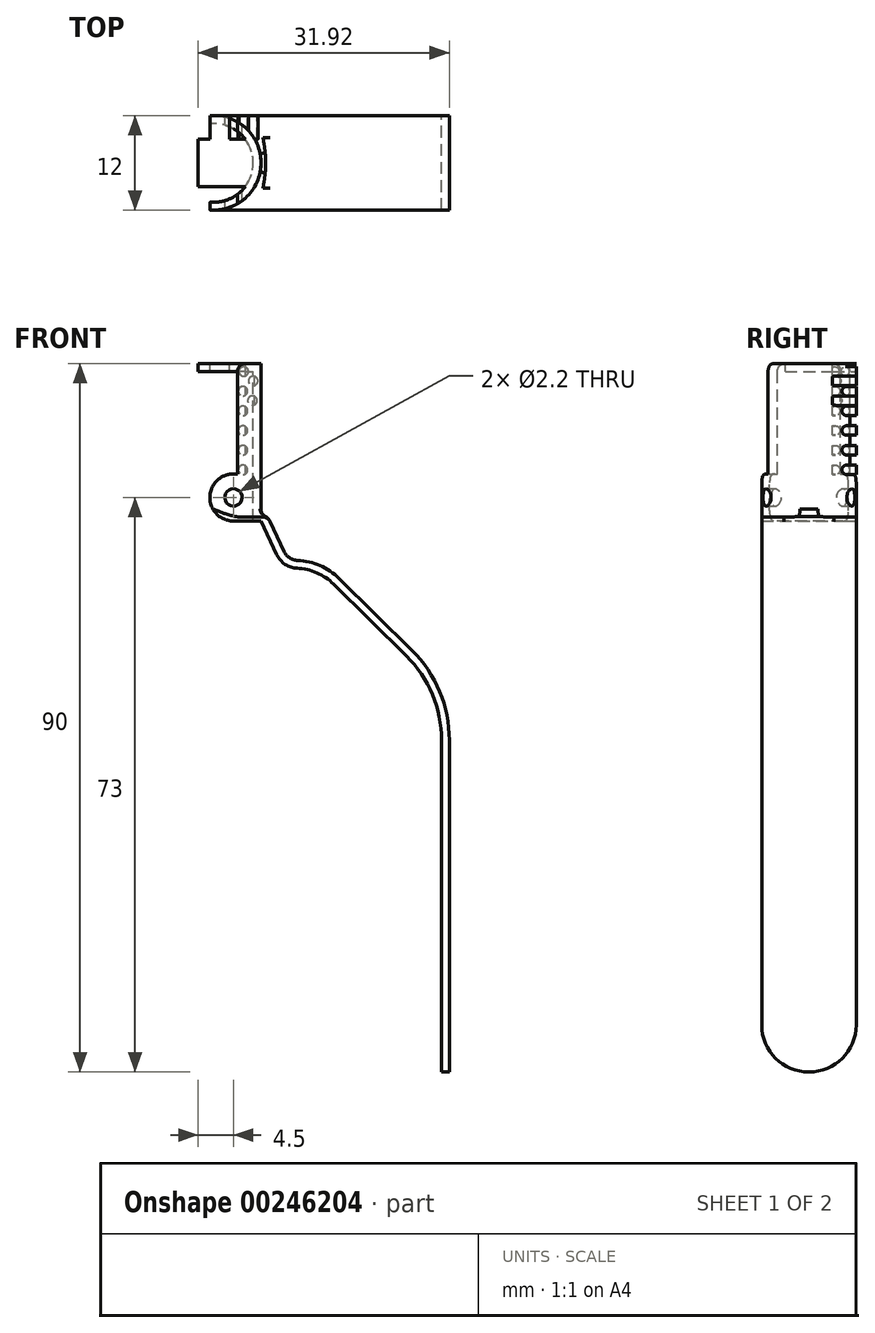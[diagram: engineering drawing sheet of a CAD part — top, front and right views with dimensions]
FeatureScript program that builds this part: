
annotation { "Feature Type Name" : "Feature", "Feature Type Description" : "" }
export const myFeature = defineFeature(function(context is Context, id is Id, definition is map)
    precondition{}
    {
        {
            var Q0;
            Q0=qCreatedBy(makeId("Front.planeOp"),FACE);
            var sketch = newSketch(context, id + "F0", { "sketchPlane" : qUnion([Q0])});
            skLineSegment(sketch, "E0", {"start": v(-3, 6) * mm, "end": v(-3, 20) * mm});
            skLineSegment(sketch, "E1", {"start": v(-3, 20) * mm, "end": v(0, 20) * mm});
            skLineSegment(sketch, "E2", {"start": v(0, 20) * mm, "end": v(0, 2.36) * mm});
            skLineSegment(sketch, "E3", {"start": v(0, 0) * mm, "end": v(-3.5, 0) * mm});
            skArc(sketch, "E4", {"start": v(-3.5, 0) * mm, "mid": v(-6.5, 3) * mm, "end": v(-3.5, 6) * mm});
            skLineSegment(sketch, "E5", {"start": v(-3.5, 6) * mm, "end": v(-3, 6) * mm});
            skLineSegment(sketch, "E6", {"start": v(0, 0) * mm, "end": v(2, -4.27) * mm});
            skArc(sketch, "E7", {"start": v(2, -4.27) * mm, "mid": v(3.05, -5.5) * mm, "end": v(4.6, -6) * mm});
            skArc(sketch, "E8", {"start": v(4.6, -6) * mm, "mid": v(7.1, -6.57) * mm, "end": v(9.22, -8.01) * mm});
            skLineSegment(sketch, "E9", {"start": v(9.22, -8.01) * mm, "end": v(18.47, -17.15) * mm});
            skArc(sketch, "E10", {"start": v(18.47, -17.15) * mm, "mid": v(21.76, -22.04) * mm, "end": v(22.92, -27.82) * mm});
            skLineSegment(sketch, "E11", {"start": v(22.92, -27.82) * mm, "end": v(22.92, -70) * mm});
            skLineSegment(sketch, "E12", {"start": v(0, 2.36) * mm, "end": v(2.62, -3.24) * mm});
            skLineSegment(sketch, "E13", {"start": v(9.92, -7.3) * mm, "end": v(19.17, -16.44) * mm});
            skArc(sketch, "E14", {"start": v(19.17, -16.44) * mm, "mid": v(22.68, -21.66) * mm, "end": v(23.92, -27.82) * mm});
            skLineSegment(sketch, "E15", {"start": v(23.92, -27.82) * mm, "end": v(23.92, -58.92) * mm});
            skArc(sketch, "E16", {"start": v(9.92, -7.3) * mm, "mid": v(7.5, -5.66) * mm, "end": v(4.63, -5) * mm});
            skArc(sketch, "E17", {"start": v(4.63, -5) * mm, "mid": v(3.6, -4.66) * mm, "end": v(2.9, -3.85) * mm});
            skLineSegment(sketch, "E18", {"start": v(2.9, -3.85) * mm, "end": v(2.62, -3.24) * mm});
            skLineSegment(sketch, "E19", {"start": v(23.92, -58.92) * mm, "end": v(23.92, -70) * mm});
            skLineSegment(sketch, "E20", {"start": v(22.92, -70) * mm, "end": v(23.92, -70) * mm});
            skCircle(sketch, "E21", {"center": v(-3.5, 3) * mm, "radius": 1.1 * mm});
            skSolve(sketch);
        }
        {
            var Q0;
            Q0=makeQuery(id+"F0.imprint","IMPRINT",FACE,{"disambiguationData":[TD([[makeQuery(id+"F0.imprint","IMPRINT",EDGE,{"derivedFrom":sQuery(id+"F0.wireOp",EDGE,"E0")}),-1.0]])]});
            extrude(context, id + "F1", {"entities" : qUnion([Q0]), "endBound" : BoundingType.SYMMETRIC, "depth" : 12 * mm});
        }
        {
            var Q0;
            Q0=makeQuery(id+"F1.opExtrude","CAP_EDGE",EDGE,{"disambiguationData":[OSD([sQuery(id+"F0.wireOp",EDGE,"E20")])],"isStart":false});
            var Q1;
            Q1=makeQuery(id+"F1.opExtrude","CAP_EDGE",EDGE,{"disambiguationData":[OSD([sQuery(id+"F0.wireOp",EDGE,"E20")])],"isStart":true});
            fillet(context, id + "F2", {"entities" : qUnion([Q0, Q1]), "radius" : 6 * mm, "tangentPropagation" : true, "allowEdgeOverflow" : false});
        }
        {
            var Q0;
            Q0=makeQuery(id+"F1.opExtrude","SWEPT_FACE",FACE,{"disambiguationData":[OSD([sQuery(id+"F0.wireOp",EDGE,"E1")])]});
            var sketch = newSketch(context, id + "F3", { "sketchPlane" : qUnion([Q0])});
            skArc(sketch, "E22", {"start": v(-6, -6) * mm, "mid": v(0, 0) * mm, "end": v(-6, 6) * mm});
            skLineSegment(sketch, "E23", {"start": v(1, -6) * mm, "end": v(-7.5, -6) * mm});
            skPoint(sketch, "E23.endSnap0", {"position": v(-1.5, -6) * mm});
            skLineSegment(sketch, "E24", {"start": v(1, 6) * mm, "end": v(-7.5, 6) * mm});
            skLineSegment(sketch, "E25", {"start": v(1, 6) * mm, "end": v(1, -6) * mm});
            skArc(sketch, "E26", {"start": v(-6, 5) * mm, "mid": v(-1, 0) * mm, "end": v(-6, -5) * mm});
            skLineSegment(sketch, "E27", {"start": v(-6, 5) * mm, "end": v(-7.5, 5) * mm});
            skLineSegment(sketch, "E28", {"start": v(-6, -5) * mm, "end": v(-7.5, -5) * mm});
            skLineSegment(sketch, "E29", {"start": v(-7.5, 5) * mm, "end": v(-7.5, -5) * mm});
            skSolve(sketch);
        }
        {
            var Q0;
            Q0 = qSketchRegion(id + "F3", true);
            extrude(context, id + "F4", {"entities" : qUnion([Q0]), "operationType" : NewBodyOperationType.REMOVE, "oppositeDirection" : true, "depth" : 19.5 * mm});
        }
        {
            var Q0;
            Q0=makeQuery(id+"F4.boolean.opBoolean","COPY",FACE,{"derivedFrom":makeQuery(id+"F4.opExtrude","CAP_FACE",FACE,{"disambiguationData":[OSD([sQuery(id+"F3.wireOp",EDGE,"E26"),sQuery(id+"F3.wireOp",EDGE,"E27"),sQuery(id+"F3.wireOp",EDGE,"E28"),sQuery(id+"F3.wireOp",EDGE,"E29")])],"isStart":false})});
            var sketch = newSketch(context, id + "F5", { "sketchPlane" : qUnion([Q0])});
            skArc(sketch, "E30", {"start": v(-5.16, -4.93) * mm, "mid": v(-1, 0) * mm, "end": v(-5.16, 4.93) * mm});
            skLineSegment(sketch, "E31", {"start": v(-5.16, 4.93) * mm, "end": v(-5.16, -4.93) * mm});
            skSolve(sketch);
        }
        {
            var Q0;
            Q0 = qSketchRegion(id + "F5", true);
            extrude(context, id + "F6", {"entities" : qUnion([Q0]), "operationType" : NewBodyOperationType.REMOVE, "oppositeDirection" : true, "depth" : 2 * mm});
        }
        {
            var Q0;
            Q0=makeQuery(id+"F1.opExtrude","SWEPT_FACE",FACE,{"disambiguationData":[OSD([sQuery(id+"F0.wireOp",EDGE,"E1")])]});
            var sketch = newSketch(context, id + "F7", { "sketchPlane" : qUnion([Q0])});
            skArc(sketch, "E32", {"start": v(-2, -3) * mm, "mid": v(-1, 0) * mm, "end": v(-2, 3) * mm});
            skLineSegment(sketch, "E33", {"start": v(-2, 3) * mm, "end": v(-8, 3) * mm});
            skLineSegment(sketch, "E34", {"start": v(-2, -3) * mm, "end": v(-8, -3) * mm});
            skLineSegment(sketch, "E35", {"start": v(-8, -3) * mm, "end": v(-8, 3) * mm});
            skSolve(sketch);
        }
        {
            var Q0;
            Q0 = qSketchRegion(id + "F7", true);
            extrude(context, id + "F8", {"entities" : qUnion([Q0]), "operationType" : NewBodyOperationType.ADD, "oppositeDirection" : true, "depth" : 1 * mm});
        }
        {
            var Q0;
            Q0=makeQuery(id+"F4.boolean.opBoolean","COPY",EDGE,{"derivedFrom":makeQuery(id+"F4.opExtrude","CAP_EDGE",EDGE,{"disambiguationData":[OSD([sQuery(id+"F3.wireOp",EDGE,"E22")])],"isStart":false})});
            fillet(context, id + "F9", {"entities" : qUnion([Q0]), "radius" : 1 * mm, "tangentPropagation" : true, "allowEdgeOverflow" : false});
        }
        {
            var Q0;
            Q0=makeQuery(id+"F4.boolean.opBoolean","INTERSECT",EDGE,{"derivedFrom":[makeQuery(id+"F1.opExtrude","SWEPT_FACE",FACE,{"disambiguationData":[OSD([sQuery(id+"F0.wireOp",EDGE,"E12"),sQuery(id+"F0.wireOp",EDGE,"E18")])]}),makeQuery(id+"F4.opExtrude","CAP_FACE",FACE,{"disambiguationData":[OSD([sQuery(id+"F3.wireOp",EDGE,"E22"),sQuery(id+"F3.wireOp",EDGE,"E23"),sQuery(id+"F3.wireOp",EDGE,"E24"),sQuery(id+"F3.wireOp",EDGE,"E25")])],"isStart":false})]});
            var Q1;
            Q1=makeQuery(id+"F9.opFillet","BLEND_EDGE",EDGE,{"blendedFrom":[makeQuery(id+"F4.boolean.opBoolean","COPY",EDGE,{"derivedFrom":makeQuery(id+"F4.opExtrude","CAP_EDGE",EDGE,{"disambiguationData":[OSD([sQuery(id+"F3.wireOp",EDGE,"E22")])],"isStart":false})}),makeQuery(id+"F1.opExtrude","SWEPT_FACE",FACE,{"disambiguationData":[OSD([sQuery(id+"F0.wireOp",EDGE,"E12"),sQuery(id+"F0.wireOp",EDGE,"E18")])]})],"blendedInto":[makeQuery(id+"F1.opExtrude","SWEPT_FACE",FACE,{"disambiguationData":[OSD([sQuery(id+"F0.wireOp",EDGE,"E12"),sQuery(id+"F0.wireOp",EDGE,"E18")])]})]});
            fillet(context, id + "F10", {"entities" : qUnion([Q0, Q1]), "radius" : 1 * mm, "tangentPropagation" : true, "allowEdgeOverflow" : false});
        }
        {
            var Q0;
            Q0=makeQuery(id+"F4.boolean.opBoolean","SPLIT",EDGE,{"disambiguationData":[OD(1.0)],"derivedFrom":makeQuery(id+"F1.opExtrude","SWEPT_EDGE",EDGE,{"disambiguationData":[OSD([sQuery(id+"F0.wireOp",EDGE,"E0"),sQuery(id+"F0.wireOp",EDGE,"E1")])]})});
            var Q1;
            Q1=makeQuery(id+"F4.boolean.opBoolean","SPLIT",EDGE,{"disambiguationData":[OD(0.0)],"derivedFrom":makeQuery(id+"F1.opExtrude","SWEPT_EDGE",EDGE,{"disambiguationData":[OSD([sQuery(id+"F0.wireOp",EDGE,"E0"),sQuery(id+"F0.wireOp",EDGE,"E1")])]})});
            fillet(context, id + "F11", {"entities" : qUnion([Q0, Q1]), "radius" : 1 * mm, "tangentPropagation" : true, "allowEdgeOverflow" : false});
        }
        {
            var Q0;
            Q0=qCreatedBy(makeId("Front.planeOp"),FACE);
            cPlane(context, id + "F12", {"entities" : qUnion([Q0]), "cplaneType" : CPlaneType.OFFSET, "offset" : 6 * mm, "oppositeDirection" : true, "width" : 150 * mm, "height" : 150 * mm});
        }
        {
            var Q0;
            Q0=qCreatedBy(id+"F12.planeOp",FACE);
            var sketch = newSketch(context, id + "F13", { "sketchPlane" : qUnion([Q0])});
            skCircle(sketch, "E36", {"center": v(-2.3, 9) * mm, "radius": 0.6 * mm});
            skCircle(sketch, "E37", {"center": v(-2.3, 14) * mm, "radius": 0.6 * mm});
            skCircle(sketch, "E38", {"center": v(-2.2, 19) * mm, "radius": 0.6 * mm});
            skCircle(sketch, "E39", {"center": v(-2.3, 16.5) * mm, "radius": 0.6 * mm});
            skCircle(sketch, "E40", {"center": v(-2.3, 11.5) * mm, "radius": 0.6 * mm});
            skCircle(sketch, "E41", {"center": v(-2.3, 6.5) * mm, "radius": 0.6 * mm});
            skLineSegment(sketch, "E42.bottom", {"start": v(-4, 20) * mm, "end": v(-6.5, 20) * mm});
            skLineSegment(sketch, "E42.top", {"start": v(-4, 19) * mm, "end": v(-6.5, 19) * mm});
            skLineSegment(sketch, "E42.left", {"start": v(-4, 20) * mm, "end": v(-4, 19) * mm});
            skLineSegment(sketch, "E42.right", {"start": v(-6.5, 20) * mm, "end": v(-6.5, 19) * mm});
            skCircle(sketch, "E43", {"center": v(-1, 17.8) * mm, "radius": 0.6 * mm});
            skCircle(sketch, "E44", {"center": v(-1.1, 15.3) * mm, "radius": 0.6 * mm});
            skSolve(sketch);
        }
        {
            var Q0;
            Q0 = qSketchRegion(id + "F13", true);
            var Q1;
            Q1=sQuery(id+"F13.wireOp",EDGE,"E38");
            var Q2;
            Q2=sQuery(id+"F13.wireOp",EDGE,"E39");
            var Q3;
            Q3=sQuery(id+"F13.wireOp",EDGE,"E37");
            var Q4;
            Q4=sQuery(id+"F13.wireOp",EDGE,"E40");
            var Q5;
            Q5=sQuery(id+"F13.wireOp",EDGE,"E36");
            var Q6;
            Q6=sQuery(id+"F13.wireOp",EDGE,"E41");
            var Q7;
            Q7=makeQuery(id+"F8.opExtrude","SWEPT_FACE",FACE,{"disambiguationData":[OSD([sQuery(id+"F7.wireOp",EDGE,"E33")])]});
            extrude(context, id + "F14", {"entities" : qUnion([Q0]), "operationType" : NewBodyOperationType.ADD, "surfaceEntities" : qUnion([Q1, Q2, Q3, Q4, Q5, Q6]), "endBound" : BoundingType.UP_TO_SURFACE, "endBoundEntityFace" : qUnion([Q7]), "depth" : 4 * mm});
        }
    });
